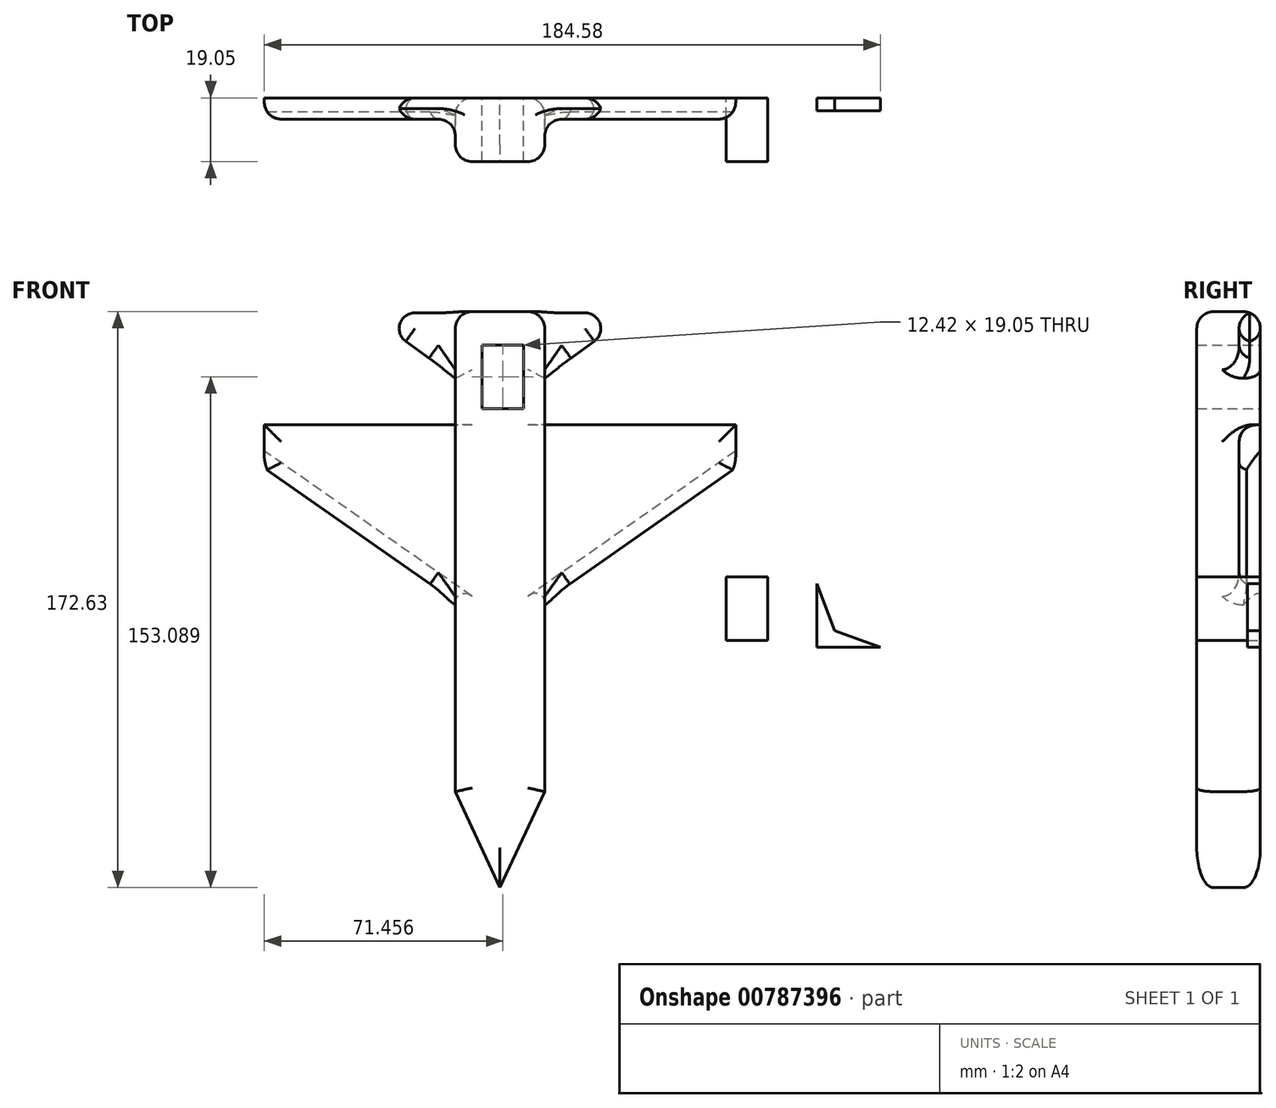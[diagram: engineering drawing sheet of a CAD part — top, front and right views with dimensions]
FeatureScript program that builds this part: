
annotation { "Feature Type Name" : "Feature", "Feature Type Description" : "" }
export const myFeature = defineFeature(function(context is Context, id is Id, definition is map)
    precondition{}
    {
        {
            var Q0;
            Q0=qCreatedBy(makeId("Front.planeOp"),FACE);
            var sketch = newSketch(context, id + "F0", { "sketchPlane" : qUnion([Q0])});
            skLineSegment(sketch, "E0", {"start": v(-28.91, -55.53) * mm, "end": v(-42.33, -26.76) * mm});
            skLineSegment(sketch, "E1", {"start": v(-42.33, -26.76) * mm, "end": v(-42.33, 29.12) * mm});
            skLineSegment(sketch, "E2", {"start": v(-42.33, 29.12) * mm, "end": v(-99.55, 69.19) * mm});
            skLineSegment(sketch, "E3", {"start": v(-99.55, 69.19) * mm, "end": v(-99.55, 83.16) * mm});
            skLineSegment(sketch, "E4", {"start": v(-99.55, 83.16) * mm, "end": v(-42.33, 83.16) * mm});
            skLineSegment(sketch, "E5", {"start": v(-42.33, 83.16) * mm, "end": v(-42.33, 97.13) * mm});
            skLineSegment(sketch, "E6", {"start": v(-42.33, 97.13) * mm, "end": v(-57.82, 108.2) * mm});
            skLineSegment(sketch, "E7", {"start": v(-57.82, 108.2) * mm, "end": v(-57.82, 117.1) * mm});
            skLineSegment(sketch, "E8", {"start": v(-57.82, 117.1) * mm, "end": v(-42.33, 117.1) * mm});
            skLineSegment(sketch, "E9", {"start": v(-28.91, -55.53) * mm, "end": v(-15.5, -26.76) * mm});
            skLineSegment(sketch, "E10", {"start": v(-15.5, -26.76) * mm, "end": v(-15.5, 29.12) * mm});
            skLineSegment(sketch, "E11", {"start": v(-15.5, 29.12) * mm, "end": v(41.72, 69.19) * mm});
            skLineSegment(sketch, "E12", {"start": v(41.72, 69.19) * mm, "end": v(41.72, 83.16) * mm});
            skPoint(sketch, "E12.endSnap0", {"position": v(-70.94, 83.16) * mm});
            skLineSegment(sketch, "E13", {"start": v(41.72, 83.16) * mm, "end": v(-15.5, 83.16) * mm});
            skLineSegment(sketch, "E14", {"start": v(-15.5, 83.16) * mm, "end": v(-15.5, 97.13) * mm});
            skLineSegment(sketch, "E15", {"start": v(-15.5, 97.13) * mm, "end": v(0, 108.2) * mm});
            skLineSegment(sketch, "E16", {"start": v(0, 108.2) * mm, "end": v(0, 117.1) * mm});
            skLineSegment(sketch, "E17", {"start": v(0, 117.1) * mm, "end": v(-15.5, 117.1) * mm});
            skPoint(sketch, "E18.endSnap0", {"position": v(-50.08, 102.67) * mm});
            skLineSegment(sketch, "E19", {"start": v(-42.33, 117.1) * mm, "end": v(-15.5, 117.1) * mm});
            skLineSegment(sketch, "E20", {"start": v(-28.91, 107.08) * mm, "end": v(-34.3, 107.08) * mm});
            skPoint(sketch, "E20.startSnap0", {"position": v(-28.91, 117.1) * mm});
            skLineSegment(sketch, "E21", {"start": v(-28.91, 107.08) * mm, "end": v(-21.88, 107.08) * mm});
            skLineSegment(sketch, "E22", {"start": v(-34.3, 107.08) * mm, "end": v(-34.3, 88.03) * mm});
            skLineSegment(sketch, "E23", {"start": v(-34.3, 88.03) * mm, "end": v(-21.88, 88.03) * mm});
            skLineSegment(sketch, "E24", {"start": v(-21.88, 88.03) * mm, "end": v(-21.88, 107.08) * mm});
            skPoint(sketch, "E25.endSnap0", {"position": v(-34.3, 97.56) * mm});
            skLineSegment(sketch, "E26", {"start": v(-42.33, 83.16) * mm, "end": v(-42.33, 29.12) * mm});
            skLineSegment(sketch, "E27", {"start": v(-15.5, 83.16) * mm, "end": v(-15.5, 29.12) * mm});
            skLineSegment(sketch, "E28", {"start": v(-42.33, 97.13) * mm, "end": v(-42.33, 117.1) * mm});
            skLineSegment(sketch, "E29", {"start": v(-15.5, 117.1) * mm, "end": v(-15.5, 97.13) * mm});
            skSolve(sketch);
        }
        {
            var Q0;
            Q0=makeQuery(id+"F0.imprint","IMPRINT",FACE,{"disambiguationData":[TD([[makeQuery(id+"F0.imprint","IMPRINT",EDGE,{"derivedFrom":sQuery(id+"F0.wireOp",EDGE,"E0")}),-1.0]])]});
            extrude(context, id + "F1", {"entities" : qUnion([Q0]), "depth" : 19.05 * mm, "offsetDistance" : 25.4 * mm});
        }
        {
            var Q0;
            Q0 = qSketchRegion(id + "F0", true);
            extrude(context, id + "F2", {"entities" : qUnion([Q0]), "operationType" : NewBodyOperationType.ADD, "depth" : 6.35 * mm, "offsetDistance" : 25.4 * mm});
        }
        {
            var Q0;
            Q0=makeQuery(id+"F1.opExtrude","CAP_EDGE",EDGE,{"disambiguationData":[OSD([sQuery(id+"F0.wireOp",EDGE,"E1"),sQuery(id+"F0.wireOp",EDGE,"E5"),sQuery(id+"F0.wireOp",EDGE,"E26"),sQuery(id+"F0.wireOp",EDGE,"E28")])],"isStart":false});
            var Q1;
            Q1=makeQuery(id+"F1.opExtrude","CAP_EDGE",EDGE,{"disambiguationData":[OSD([sQuery(id+"F0.wireOp",EDGE,"E10"),sQuery(id+"F0.wireOp",EDGE,"E14"),sQuery(id+"F0.wireOp",EDGE,"E27"),sQuery(id+"F0.wireOp",EDGE,"E29")])],"isStart":false});
            var Q2;
            {var subQ0=sQuery(id+"F0.wireOp",EDGE,"E14");var subQ1=sQuery(id+"F0.wireOp",EDGE,"E10");Q2=makeQuery(id+"F2.boolean.opBoolean","INTERSECT",EDGE,{"disambiguationData":[OD(0.0)],"derivedFrom":[makeQuery(id+"F1.opExtrude","SWEPT_FACE",FACE,{"disambiguationData":[OSD([subQ1,subQ0,sQuery(id+"F0.wireOp",EDGE,"E27"),sQuery(id+"F0.wireOp",EDGE,"E29")])]}),makeQuery(id+"F2.opExtrude","CAP_FACE",FACE,{"disambiguationData":[OSD([sQuery(id+"F0.wireOp",EDGE,"E0"),sQuery(id+"F0.wireOp",EDGE,"E1"),sQuery(id+"F0.wireOp",EDGE,"E2"),sQuery(id+"F0.wireOp",EDGE,"E3"),sQuery(id+"F0.wireOp",EDGE,"E4"),sQuery(id+"F0.wireOp",EDGE,"E5"),sQuery(id+"F0.wireOp",EDGE,"E6"),sQuery(id+"F0.wireOp",EDGE,"E7"),sQuery(id+"F0.wireOp",EDGE,"E8"),sQuery(id+"F0.wireOp",EDGE,"E9"),subQ1,sQuery(id+"F0.wireOp",EDGE,"E11"),sQuery(id+"F0.wireOp",EDGE,"E12"),sQuery(id+"F0.wireOp",EDGE,"E13"),subQ0,sQuery(id+"F0.wireOp",EDGE,"E15"),sQuery(id+"F0.wireOp",EDGE,"E16"),sQuery(id+"F0.wireOp",EDGE,"E17"),sQuery(id+"F0.wireOp",EDGE,"E19"),sQuery(id+"F0.wireOp",EDGE,"E20"),sQuery(id+"F0.wireOp",EDGE,"E21"),sQuery(id+"F0.wireOp",EDGE,"E22"),sQuery(id+"F0.wireOp",EDGE,"E23"),sQuery(id+"F0.wireOp",EDGE,"E24")])],"isStart":false})]});}
            var Q3;
            {var subQ0=sQuery(id+"F0.wireOp",EDGE,"E5");var subQ1=sQuery(id+"F0.wireOp",EDGE,"E1");Q3=makeQuery(id+"F2.boolean.opBoolean","INTERSECT",EDGE,{"disambiguationData":[OD(0.0)],"derivedFrom":[makeQuery(id+"F1.opExtrude","SWEPT_FACE",FACE,{"disambiguationData":[OSD([subQ1,subQ0,sQuery(id+"F0.wireOp",EDGE,"E26"),sQuery(id+"F0.wireOp",EDGE,"E28")])]}),makeQuery(id+"F2.opExtrude","CAP_FACE",FACE,{"disambiguationData":[OSD([sQuery(id+"F0.wireOp",EDGE,"E0"),subQ1,sQuery(id+"F0.wireOp",EDGE,"E2"),sQuery(id+"F0.wireOp",EDGE,"E3"),sQuery(id+"F0.wireOp",EDGE,"E4"),subQ0,sQuery(id+"F0.wireOp",EDGE,"E6"),sQuery(id+"F0.wireOp",EDGE,"E7"),sQuery(id+"F0.wireOp",EDGE,"E8"),sQuery(id+"F0.wireOp",EDGE,"E9"),sQuery(id+"F0.wireOp",EDGE,"E10"),sQuery(id+"F0.wireOp",EDGE,"E11"),sQuery(id+"F0.wireOp",EDGE,"E12"),sQuery(id+"F0.wireOp",EDGE,"E13"),sQuery(id+"F0.wireOp",EDGE,"E14"),sQuery(id+"F0.wireOp",EDGE,"E15"),sQuery(id+"F0.wireOp",EDGE,"E16"),sQuery(id+"F0.wireOp",EDGE,"E17"),sQuery(id+"F0.wireOp",EDGE,"E19"),sQuery(id+"F0.wireOp",EDGE,"E20"),sQuery(id+"F0.wireOp",EDGE,"E21"),sQuery(id+"F0.wireOp",EDGE,"E22"),sQuery(id+"F0.wireOp",EDGE,"E23"),sQuery(id+"F0.wireOp",EDGE,"E24")])],"isStart":false})]});}
            var Q4;
            {var subQ0=sQuery(id+"F0.wireOp",EDGE,"E5");var subQ1=sQuery(id+"F0.wireOp",EDGE,"E1");Q4=makeQuery(id+"F2.boolean.opBoolean","INTERSECT",EDGE,{"disambiguationData":[OD(1.0)],"derivedFrom":[makeQuery(id+"F1.opExtrude","SWEPT_FACE",FACE,{"disambiguationData":[OSD([subQ1,subQ0,sQuery(id+"F0.wireOp",EDGE,"E26"),sQuery(id+"F0.wireOp",EDGE,"E28")])]}),makeQuery(id+"F2.opExtrude","CAP_FACE",FACE,{"disambiguationData":[OSD([sQuery(id+"F0.wireOp",EDGE,"E0"),subQ1,sQuery(id+"F0.wireOp",EDGE,"E2"),sQuery(id+"F0.wireOp",EDGE,"E3"),sQuery(id+"F0.wireOp",EDGE,"E4"),subQ0,sQuery(id+"F0.wireOp",EDGE,"E6"),sQuery(id+"F0.wireOp",EDGE,"E7"),sQuery(id+"F0.wireOp",EDGE,"E8"),sQuery(id+"F0.wireOp",EDGE,"E9"),sQuery(id+"F0.wireOp",EDGE,"E10"),sQuery(id+"F0.wireOp",EDGE,"E11"),sQuery(id+"F0.wireOp",EDGE,"E12"),sQuery(id+"F0.wireOp",EDGE,"E13"),sQuery(id+"F0.wireOp",EDGE,"E14"),sQuery(id+"F0.wireOp",EDGE,"E15"),sQuery(id+"F0.wireOp",EDGE,"E16"),sQuery(id+"F0.wireOp",EDGE,"E17"),sQuery(id+"F0.wireOp",EDGE,"E19"),sQuery(id+"F0.wireOp",EDGE,"E20"),sQuery(id+"F0.wireOp",EDGE,"E21"),sQuery(id+"F0.wireOp",EDGE,"E22"),sQuery(id+"F0.wireOp",EDGE,"E23"),sQuery(id+"F0.wireOp",EDGE,"E24")])],"isStart":false})]});}
            var Q5;
            {var subQ0=sQuery(id+"F0.wireOp",EDGE,"E14");var subQ1=sQuery(id+"F0.wireOp",EDGE,"E10");Q5=makeQuery(id+"F2.boolean.opBoolean","INTERSECT",EDGE,{"disambiguationData":[OD(1.0)],"derivedFrom":[makeQuery(id+"F1.opExtrude","SWEPT_FACE",FACE,{"disambiguationData":[OSD([subQ1,subQ0,sQuery(id+"F0.wireOp",EDGE,"E27"),sQuery(id+"F0.wireOp",EDGE,"E29")])]}),makeQuery(id+"F2.opExtrude","CAP_FACE",FACE,{"disambiguationData":[OSD([sQuery(id+"F0.wireOp",EDGE,"E0"),sQuery(id+"F0.wireOp",EDGE,"E1"),sQuery(id+"F0.wireOp",EDGE,"E2"),sQuery(id+"F0.wireOp",EDGE,"E3"),sQuery(id+"F0.wireOp",EDGE,"E4"),sQuery(id+"F0.wireOp",EDGE,"E5"),sQuery(id+"F0.wireOp",EDGE,"E6"),sQuery(id+"F0.wireOp",EDGE,"E7"),sQuery(id+"F0.wireOp",EDGE,"E8"),sQuery(id+"F0.wireOp",EDGE,"E9"),subQ1,sQuery(id+"F0.wireOp",EDGE,"E11"),sQuery(id+"F0.wireOp",EDGE,"E12"),sQuery(id+"F0.wireOp",EDGE,"E13"),subQ0,sQuery(id+"F0.wireOp",EDGE,"E15"),sQuery(id+"F0.wireOp",EDGE,"E16"),sQuery(id+"F0.wireOp",EDGE,"E17"),sQuery(id+"F0.wireOp",EDGE,"E19"),sQuery(id+"F0.wireOp",EDGE,"E20"),sQuery(id+"F0.wireOp",EDGE,"E21"),sQuery(id+"F0.wireOp",EDGE,"E22"),sQuery(id+"F0.wireOp",EDGE,"E23"),sQuery(id+"F0.wireOp",EDGE,"E24")])],"isStart":false})]});}
            var Q6;
            Q6=makeQuery(id+"F1.opExtrude","CAP_EDGE",EDGE,{"disambiguationData":[OSD([sQuery(id+"F0.wireOp",EDGE,"E0")])],"isStart":false});
            var Q7;
            Q7=makeQuery(id+"F1.opExtrude","CAP_EDGE",EDGE,{"disambiguationData":[OSD([sQuery(id+"F0.wireOp",EDGE,"E9")])],"isStart":false});
            var Q8;
            Q8=makeQuery(id+"F1.opExtrude","CAP_EDGE",EDGE,{"disambiguationData":[OSD([sQuery(id+"F0.wireOp",EDGE,"E0")])],"isStart":true});
            var Q9;
            {var subQ9=sQuery(id+"F0.wireOp",EDGE,"E5");var subQ11=sQuery(id+"F0.wireOp",EDGE,"E1");var subQ12=sQuery(id+"F0.wireOp",EDGE,"E0");var subQ13=sQuery(id+"F0.wireOp",EDGE,"E28");var subQ14=sQuery(id+"F0.wireOp",EDGE,"E26");Q9=makeQuery(id+"F2.boolean.opBoolean","SPLIT",EDGE,{"disambiguationData":[TD([makeQuery(id+"F1.opExtrude","SWEPT_FACE",FACE,{"disambiguationData":[OSD([subQ12])]})])],"derivedFrom":makeQuery(id+"F1.opExtrude","CAP_EDGE",EDGE,{"disambiguationData":[OSD([subQ11,subQ9,subQ14,subQ13])],"isStart":true})});}
            var Q10;
            {var subQ6=sQuery(id+"F0.wireOp",EDGE,"E14");var subQ8=sQuery(id+"F0.wireOp",EDGE,"E10");var subQ9=sQuery(id+"F0.wireOp",EDGE,"E9");var subQ13=sQuery(id+"F0.wireOp",EDGE,"E29");var subQ14=sQuery(id+"F0.wireOp",EDGE,"E27");Q10=makeQuery(id+"F2.boolean.opBoolean","SPLIT",EDGE,{"disambiguationData":[TD([makeQuery(id+"F1.opExtrude","SWEPT_FACE",FACE,{"disambiguationData":[OSD([subQ9])]})])],"derivedFrom":makeQuery(id+"F1.opExtrude","CAP_EDGE",EDGE,{"disambiguationData":[OSD([subQ8,subQ6,subQ14,subQ13])],"isStart":true})});}
            var Q11;
            Q11=makeQuery(id+"F1.opExtrude","CAP_EDGE",EDGE,{"disambiguationData":[OSD([sQuery(id+"F0.wireOp",EDGE,"E9")])],"isStart":true});
            fillet(context, id + "F3", {"entities" : qUnion([Q0, Q1, Q2, Q3, Q4, Q5, Q6, Q7, Q8, Q9, Q10, Q11]), "radius" : 5.08 * mm, "tangentPropagation" : true, "allowEdgeOverflow" : false});
        }
        {
            var Q0;
            Q0=qCreatedBy(makeId("Front.planeOp"),FACE);
            var sketch = newSketch(context, id + "F4", { "sketchPlane" : qUnion([Q0])});
            skLineSegment(sketch, "E30.bottom", {"start": v(38.82, 37.56) * mm, "end": v(51.24, 37.56) * mm});
            skLineSegment(sketch, "E30.top", {"start": v(38.82, 18.51) * mm, "end": v(51.24, 18.51) * mm});
            skLineSegment(sketch, "E30.left", {"start": v(38.82, 37.56) * mm, "end": v(38.82, 18.51) * mm});
            skLineSegment(sketch, "E30.right", {"start": v(51.24, 37.56) * mm, "end": v(51.24, 18.51) * mm});
            skLineSegment(sketch, "E31", {"start": v(84.33, 32.76) * mm, "end": v(84.33, 13.7) * mm});
            skLineSegment(sketch, "E32", {"start": v(84.33, 13.7) * mm, "end": v(103.38, 13.7) * mm});
            skLineSegment(sketch, "E33", {"start": v(103.38, 13.7) * mm, "end": v(91.58, 21.1) * mm});
            skLineSegment(sketch, "E34", {"start": v(91.58, 21.1) * mm, "end": v(84.33, 32.76) * mm});
            skSolve(sketch);
        }
        {
            var Q0;
            Q0=makeQuery(id+"F4.imprint","IMPRINT",FACE,{"disambiguationData":[TD([[makeQuery(id+"F4.imprint","IMPRINT",EDGE,{"derivedFrom":sQuery(id+"F4.wireOp",EDGE,"E30.bottom")}),-1.0]])]});
            extrude(context, id + "F5", {"entities" : qUnion([Q0]), "depth" : 19.05 * mm, "offsetDistance" : 25.4 * mm});
        }
        {
            var Q0;
            Q0=qCreatedBy(makeId("Front.planeOp"),FACE);
            var sketch = newSketch(context, id + "F6", { "sketchPlane" : qUnion([Q0])});
            skLineSegment(sketch, "E35", {"start": v(65.98, 35.54) * mm, "end": v(65.98, 16.5) * mm});
            skLineSegment(sketch, "E36", {"start": v(65.98, 16.5) * mm, "end": v(85.03, 16.5) * mm});
            skLineSegment(sketch, "E37", {"start": v(85.03, 16.5) * mm, "end": v(71.32, 21.48) * mm});
            skLineSegment(sketch, "E38", {"start": v(71.32, 21.48) * mm, "end": v(65.98, 35.54) * mm});
            skSolve(sketch);
        }
        {
            var Q0;
            Q0 = qSketchRegion(id + "F6", true);
            extrude(context, id + "F7", {"entities" : qUnion([Q0]), "depth" : 3.8 * mm, "offsetDistance" : 25.4 * mm});
        }
        {
            var Q0;
            Q0=makeQuery(id+"F2.opExtrude","CAP_EDGE",EDGE,{"disambiguationData":[OSD([sQuery(id+"F0.wireOp",EDGE,"E15")])],"isStart":true});
            var Q1;
            Q1=makeQuery(id+"F2.opExtrude","CAP_EDGE",EDGE,{"disambiguationData":[OSD([sQuery(id+"F0.wireOp",EDGE,"E15")])],"isStart":false});
            var Q2;
            Q2=makeQuery(id+"F2.opExtrude","CAP_EDGE",EDGE,{"disambiguationData":[OSD([sQuery(id+"F0.wireOp",EDGE,"E6")])],"isStart":true});
            var Q3;
            Q3=makeQuery(id+"F2.opExtrude","CAP_EDGE",EDGE,{"disambiguationData":[OSD([sQuery(id+"F0.wireOp",EDGE,"E6")])],"isStart":false});
            fillet(context, id + "F8", {"entities" : qUnion([Q0, Q1, Q2, Q3]), "radius" : 5.08 * mm, "tangentPropagation" : true, "allowEdgeOverflow" : false});
        }
        {
            var Q0;
            {var subQ0=sQuery(id+"F0.wireOp",EDGE,"E4");var subQ11=sQuery(id+"F0.wireOp",EDGE,"E5");var subQ12=sQuery(id+"F0.wireOp",EDGE,"E1");var subQ14=sQuery(id+"F0.wireOp",EDGE,"E28");var subQ15=sQuery(id+"F0.wireOp",EDGE,"E26");Q0=makeQuery(id+"F2.boolean.opBoolean","SPLIT",EDGE,{"disambiguationData":[TD([makeQuery(id+"F2.opExtrude","SWEPT_FACE",FACE,{"disambiguationData":[OSD([subQ0])]})])],"derivedFrom":makeQuery(id+"F1.opExtrude","CAP_EDGE",EDGE,{"disambiguationData":[OSD([subQ12,subQ11,subQ15,subQ14])],"isStart":true})});}
            var Q1;
            {var subQ7=sQuery(id+"F0.wireOp",EDGE,"E14");var subQ8=sQuery(id+"F0.wireOp",EDGE,"E13");var subQ9=sQuery(id+"F0.wireOp",EDGE,"E10");var subQ14=sQuery(id+"F0.wireOp",EDGE,"E29");var subQ15=sQuery(id+"F0.wireOp",EDGE,"E27");Q1=makeQuery(id+"F2.boolean.opBoolean","SPLIT",EDGE,{"disambiguationData":[TD([makeQuery(id+"F2.opExtrude","SWEPT_FACE",FACE,{"disambiguationData":[OSD([subQ8])]})])],"derivedFrom":makeQuery(id+"F1.opExtrude","CAP_EDGE",EDGE,{"disambiguationData":[OSD([subQ9,subQ7,subQ15,subQ14])],"isStart":true})});}
            var Q2;
            {var subQ0=sQuery(id+"F0.wireOp",EDGE,"E19");Q2=makeQuery(id+"F2.boolean.opBoolean","MERGE",EDGE,{"derivedFrom":[makeQuery(id+"F1.opExtrude","CAP_EDGE",EDGE,{"disambiguationData":[OSD([subQ0])],"isStart":true}),makeQuery(id+"F2.opExtrude","CAP_EDGE",EDGE,{"disambiguationData":[OSD([sQuery(id+"F0.wireOp",EDGE,"E8"),sQuery(id+"F0.wireOp",EDGE,"E17"),subQ0])],"isStart":true})]});}
            var Q3;
            {var subQ0=sQuery(id+"F0.wireOp",EDGE,"E19");Q3=makeQuery(id+"F2.boolean.opBoolean","MERGE",FACE,{"derivedFrom":[makeQuery(id+"F1.opExtrude","SWEPT_FACE",FACE,{"disambiguationData":[OSD([subQ0])]}),makeQuery(id+"F2.opExtrude","SWEPT_FACE",FACE,{"disambiguationData":[OSD([sQuery(id+"F0.wireOp",EDGE,"E8"),sQuery(id+"F0.wireOp",EDGE,"E17"),subQ0])]})]});}
            fillet(context, id + "F9", {"entities" : qUnion([Q0, Q1, Q2, Q3]), "radius" : 5.08 * mm, "tangentPropagation" : true, "allowEdgeOverflow" : false});
        }
        {
            var Q0;
            Q0=makeQuery(id+"F2.opExtrude","CAP_EDGE",EDGE,{"disambiguationData":[OSD([sQuery(id+"F0.wireOp",EDGE,"E11")])],"isStart":false});
            var Q1;
            {var subQ0=sQuery(id+"F0.wireOp",EDGE,"E14");var subQ1=sQuery(id+"F0.wireOp",EDGE,"E10");var subQ2=sQuery(id+"F0.wireOp",EDGE,"E12");var subQ3=sQuery(id+"F0.wireOp",EDGE,"E11");var subQ4=sQuery(id+"F0.wireOp",EDGE,"E13");Q1=makeQuery(id+"F2.boolean.opBoolean","SPLIT",FACE,{"disambiguationData":[TD([makeQuery(id+"F2.opExtrude","SWEPT_FACE",FACE,{"disambiguationData":[OSD([subQ3])]})])],"derivedFrom":makeQuery(id+"F2.opExtrude","CAP_FACE",FACE,{"disambiguationData":[OSD([sQuery(id+"F0.wireOp",EDGE,"E0"),sQuery(id+"F0.wireOp",EDGE,"E1"),sQuery(id+"F0.wireOp",EDGE,"E2"),sQuery(id+"F0.wireOp",EDGE,"E3"),sQuery(id+"F0.wireOp",EDGE,"E4"),sQuery(id+"F0.wireOp",EDGE,"E5"),sQuery(id+"F0.wireOp",EDGE,"E6"),sQuery(id+"F0.wireOp",EDGE,"E7"),sQuery(id+"F0.wireOp",EDGE,"E8"),sQuery(id+"F0.wireOp",EDGE,"E9"),subQ1,subQ3,subQ2,subQ4,subQ0,sQuery(id+"F0.wireOp",EDGE,"E15"),sQuery(id+"F0.wireOp",EDGE,"E16"),sQuery(id+"F0.wireOp",EDGE,"E17"),sQuery(id+"F0.wireOp",EDGE,"E19"),sQuery(id+"F0.wireOp",EDGE,"E20"),sQuery(id+"F0.wireOp",EDGE,"E21"),sQuery(id+"F0.wireOp",EDGE,"E22"),sQuery(id+"F0.wireOp",EDGE,"E23"),sQuery(id+"F0.wireOp",EDGE,"E24")])],"isStart":false})});}
            var Q2;
            {var subQ0=sQuery(id+"F0.wireOp",EDGE,"E5");var subQ1=sQuery(id+"F0.wireOp",EDGE,"E1");var subQ2=sQuery(id+"F0.wireOp",EDGE,"E2");var subQ3=sQuery(id+"F0.wireOp",EDGE,"E3");var subQ4=sQuery(id+"F0.wireOp",EDGE,"E4");Q2=makeQuery(id+"F2.boolean.opBoolean","SPLIT",FACE,{"disambiguationData":[TD([makeQuery(id+"F2.opExtrude","SWEPT_FACE",FACE,{"disambiguationData":[OSD([subQ2])]})])],"derivedFrom":makeQuery(id+"F2.opExtrude","CAP_FACE",FACE,{"disambiguationData":[OSD([sQuery(id+"F0.wireOp",EDGE,"E0"),subQ1,subQ2,subQ3,subQ4,subQ0,sQuery(id+"F0.wireOp",EDGE,"E6"),sQuery(id+"F0.wireOp",EDGE,"E7"),sQuery(id+"F0.wireOp",EDGE,"E8"),sQuery(id+"F0.wireOp",EDGE,"E9"),sQuery(id+"F0.wireOp",EDGE,"E10"),sQuery(id+"F0.wireOp",EDGE,"E11"),sQuery(id+"F0.wireOp",EDGE,"E12"),sQuery(id+"F0.wireOp",EDGE,"E13"),sQuery(id+"F0.wireOp",EDGE,"E14"),sQuery(id+"F0.wireOp",EDGE,"E15"),sQuery(id+"F0.wireOp",EDGE,"E16"),sQuery(id+"F0.wireOp",EDGE,"E17"),sQuery(id+"F0.wireOp",EDGE,"E19"),sQuery(id+"F0.wireOp",EDGE,"E20"),sQuery(id+"F0.wireOp",EDGE,"E21"),sQuery(id+"F0.wireOp",EDGE,"E22"),sQuery(id+"F0.wireOp",EDGE,"E23"),sQuery(id+"F0.wireOp",EDGE,"E24")])],"isStart":false})});}
            fillet(context, id + "F10", {"entities" : qUnion([Q0, Q1, Q2]), "radius" : 5.08 * mm, "tangentPropagation" : true, "allowEdgeOverflow" : false});
        }
        {
            var Q0;
            Q0=makeQuery(id+"F2.opExtrude","CAP_EDGE",EDGE,{"disambiguationData":[OSD([sQuery(id+"F0.wireOp",EDGE,"E11")])],"isStart":true});
            var Q1;
            Q1=makeQuery(id+"F2.opExtrude","CAP_EDGE",EDGE,{"disambiguationData":[OSD([sQuery(id+"F0.wireOp",EDGE,"E2")])],"isStart":true});
            chamfer(context, id + "F11", {"entities" : qUnion([Q0, Q1]), "width" : 5.08 * mm, "tangentPropagation" : true});
        }
    });
